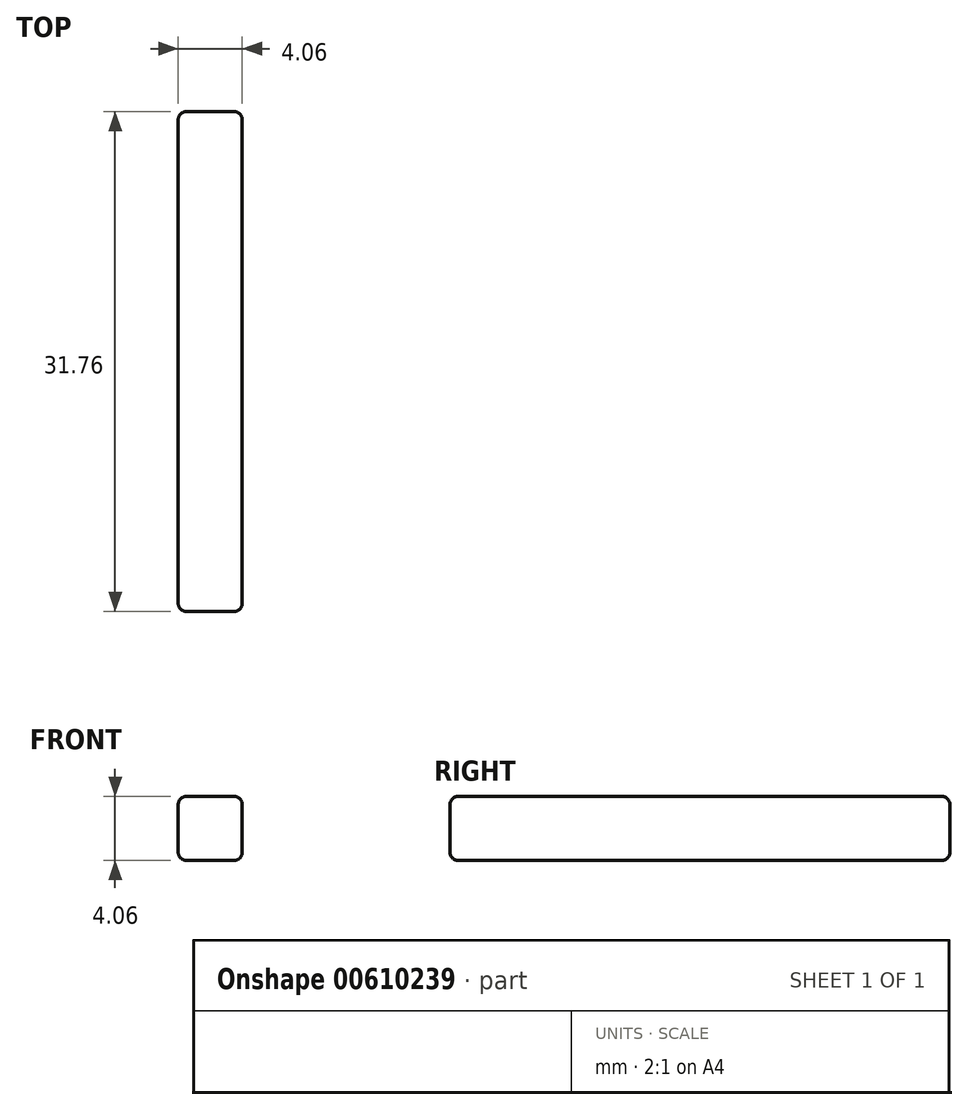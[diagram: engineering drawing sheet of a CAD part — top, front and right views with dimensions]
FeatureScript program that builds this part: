
annotation { "Feature Type Name" : "Feature", "Feature Type Description" : "" }
export const myFeature = defineFeature(function(context is Context, id is Id, definition is map)
    precondition{}
    {
        {
            var Q0;
            Q0=qCreatedBy(makeId("Front.planeOp"),FACE);
            var sketch = newSketch(context, id + "F0", { "sketchPlane" : qUnion([Q0])});
            skLineSegment(sketch, "E0.bottom", {"start": v(1.52, 2.03) * mm, "end": v(-1.52, 2.03) * mm});
            skLineSegment(sketch, "E0.top", {"start": v(1.52, -2.03) * mm, "end": v(-1.52, -2.03) * mm});
            skLineSegment(sketch, "E0.left", {"start": v(2.03, 1.52) * mm, "end": v(2.03, -1.52) * mm});
            skLineSegment(sketch, "E0.right", {"start": v(-2.03, 1.52) * mm, "end": v(-2.03, -1.52) * mm});
            skPoint(sketch, "E0.middle", {"position": v(0, 0) * mm});
            skPoint(sketch, "E1.visualSharp", {"position": v(2.03, 2.03) * mm});
            skArc(sketch, "E1.filletArc", {"start": v(2.03, 1.52) * mm, "mid": v(1.88, 1.88) * mm, "end": v(1.52, 2.03) * mm});
            skPoint(sketch, "E2.visualSharp", {"position": v(-2.03, 2.03) * mm});
            skArc(sketch, "E2.filletArc", {"start": v(-1.52, 2.03) * mm, "mid": v(-1.88, 1.88) * mm, "end": v(-2.03, 1.52) * mm});
            skPoint(sketch, "E3.visualSharp", {"position": v(-2.03, -2.03) * mm});
            skArc(sketch, "E3.filletArc", {"start": v(-2.03, -1.52) * mm, "mid": v(-1.88, -1.88) * mm, "end": v(-1.52, -2.03) * mm});
            skPoint(sketch, "E4.visualSharp", {"position": v(2.03, -2.03) * mm});
            skArc(sketch, "E4.filletArc", {"start": v(1.52, -2.03) * mm, "mid": v(1.88, -1.88) * mm, "end": v(2.03, -1.52) * mm});
            skSolve(sketch);
        }
        {
            var Q0;
            Q0=makeQuery(id+"F0.imprint","IMPRINT",FACE,{"disambiguationData":[TD([[makeQuery(id+"F0.imprint","IMPRINT",EDGE,{"derivedFrom":sQuery(id+"F0.wireOp",EDGE,"E0.bottom")}),1.0]])]});
            extrude(context, id + "F1", {"entities" : qUnion([Q0]), "endBound" : BoundingType.SYMMETRIC, "depth" : 31.75 * mm, "offsetDistance" : 25.4 * mm});
        }
        {
            var Q0;
            Q0=makeQuery(id+"F1.opExtrude","CAP_FACE",FACE,{"disambiguationData":[OSD([sQuery(id+"F0.wireOp",EDGE,"E0.bottom"),sQuery(id+"F0.wireOp",EDGE,"E0.top"),sQuery(id+"F0.wireOp",EDGE,"E0.left"),sQuery(id+"F0.wireOp",EDGE,"E0.right"),sQuery(id+"F0.wireOp",EDGE,"E1.filletArc"),sQuery(id+"F0.wireOp",EDGE,"E2.filletArc"),sQuery(id+"F0.wireOp",EDGE,"E3.filletArc"),sQuery(id+"F0.wireOp",EDGE,"E4.filletArc")])],"isStart":false});
            var Q1;
            Q1=makeQuery(id+"F1.opExtrude","CAP_FACE",FACE,{"disambiguationData":[OSD([sQuery(id+"F0.wireOp",EDGE,"E0.bottom"),sQuery(id+"F0.wireOp",EDGE,"E0.top"),sQuery(id+"F0.wireOp",EDGE,"E0.left"),sQuery(id+"F0.wireOp",EDGE,"E0.right"),sQuery(id+"F0.wireOp",EDGE,"E1.filletArc"),sQuery(id+"F0.wireOp",EDGE,"E2.filletArc"),sQuery(id+"F0.wireOp",EDGE,"E3.filletArc"),sQuery(id+"F0.wireOp",EDGE,"E4.filletArc")])],"isStart":true});
            fillet(context, id + "F2", {"entities" : qUnion([Q0, Q1]), "radius" : 0.5 * mm, "tangentPropagation" : true, "allowEdgeOverflow" : false});
        }
    });
